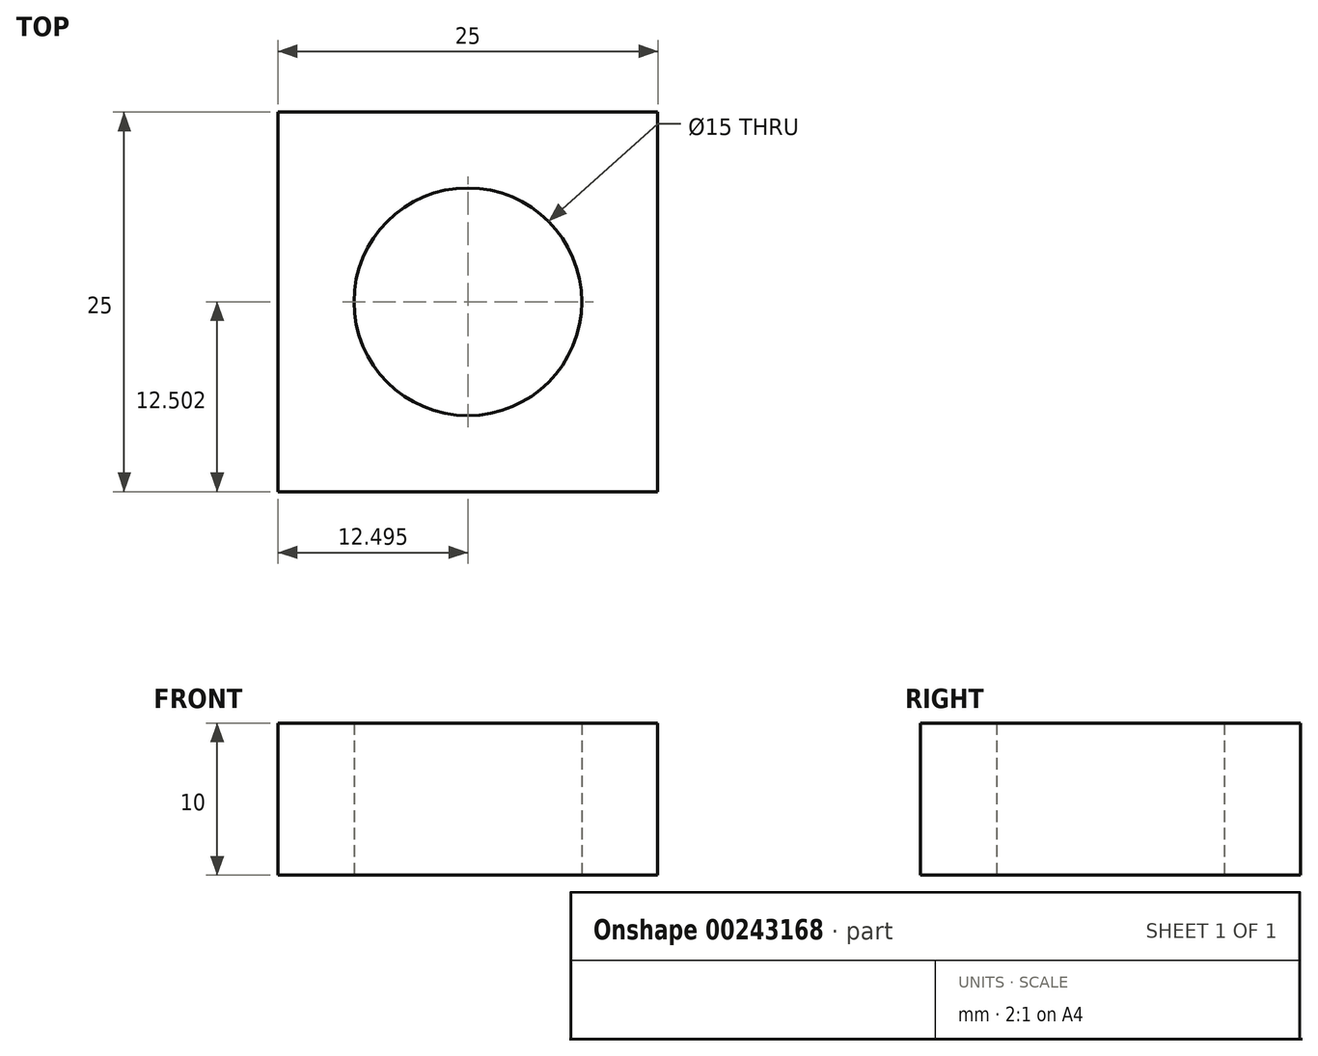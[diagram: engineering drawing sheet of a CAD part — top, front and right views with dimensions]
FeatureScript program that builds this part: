
annotation { "Feature Type Name" : "Feature", "Feature Type Description" : "" }
export const myFeature = defineFeature(function(context is Context, id is Id, definition is map)
    precondition{}
    {
        {
            var Q0;
            Q0=qCreatedBy(makeId("Top.planeOp"),FACE);
            var sketch = newSketch(context, id + "F0", { "sketchPlane" : qUnion([Q0])});
            skLineSegment(sketch, "E0.bottom", {"start": v(-7.5, 0.6) * mm, "end": v(17.5, 0.6) * mm});
            skLineSegment(sketch, "E0.top", {"start": v(-7.5, -24.4) * mm, "end": v(17.5, -24.4) * mm});
            skLineSegment(sketch, "E0.left", {"start": v(-7.5, 0.6) * mm, "end": v(-7.5, -24.4) * mm});
            skLineSegment(sketch, "E0.right", {"start": v(17.5, 0.6) * mm, "end": v(17.5, -24.4) * mm});
            skCircle(sketch, "E1", {"center": v(5, -11.9) * mm, "radius": 7.5 * mm});
            skSolve(sketch);
        }
        {
            var Q0;
            Q0=makeQuery(id+"F0.imprint","IMPRINT",FACE,{"disambiguationData":[TD([[makeQuery(id+"F0.imprint","IMPRINT",EDGE,{"derivedFrom":sQuery(id+"F0.wireOp",EDGE,"E0.bottom")}),-1.0]])]});
            extrude(context, id + "F1", {"entities" : qUnion([Q0]), "depth" : 10 * mm});
        }
    });
